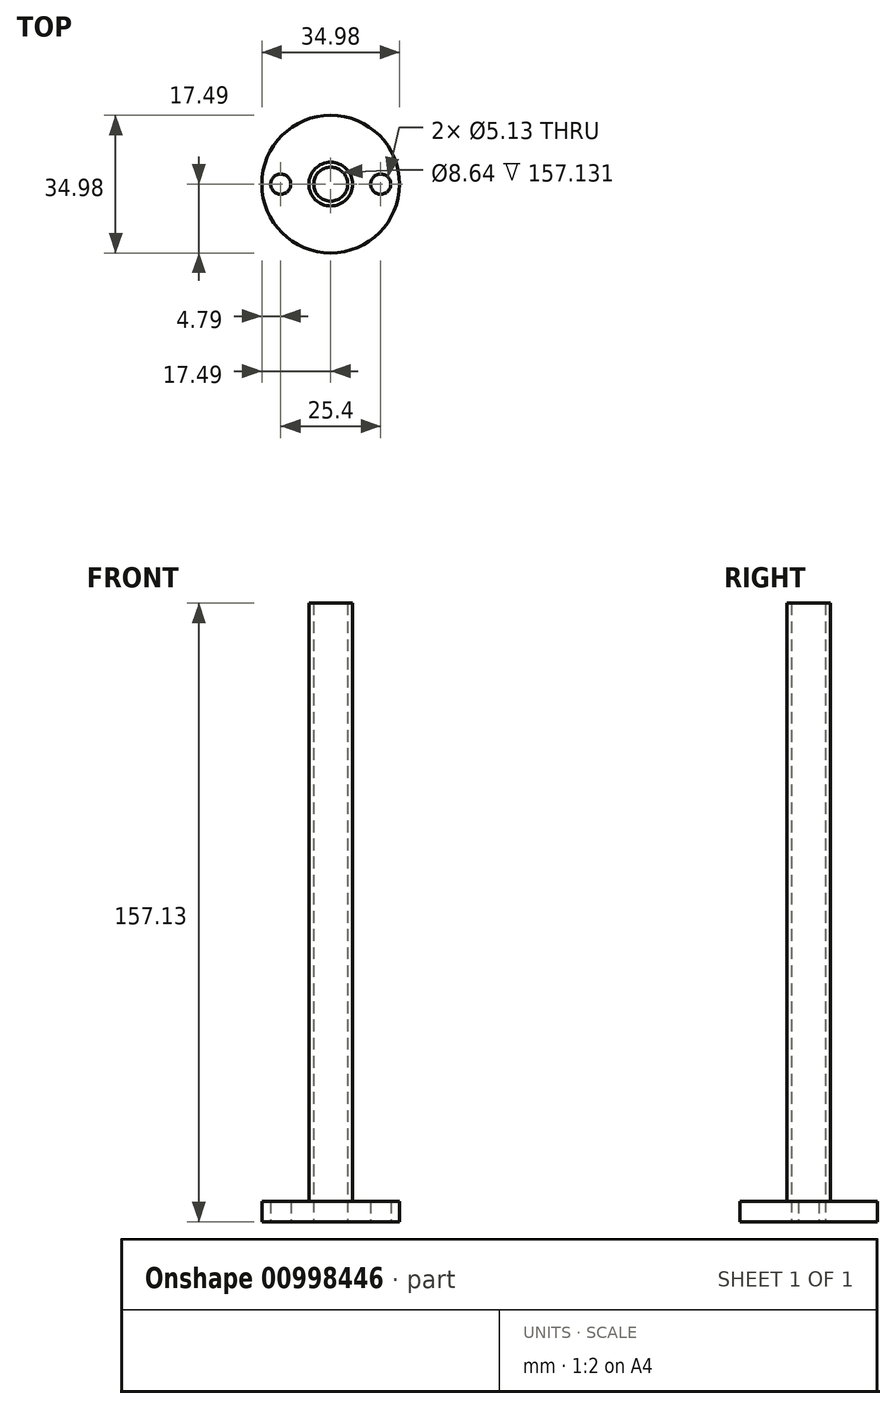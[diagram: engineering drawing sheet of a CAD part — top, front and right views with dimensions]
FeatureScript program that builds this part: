
annotation { "Feature Type Name" : "Feature", "Feature Type Description" : "" }
export const myFeature = defineFeature(function(context is Context, id is Id, definition is map)
    precondition{}
    {
        {
            var Q0;
            Q0=qCreatedBy(makeId("Top.planeOp"),FACE);
            var sketch = newSketch(context, id + "F0", { "sketchPlane" : qUnion([Q0])});
            skCircle(sketch, "E0", {"center": v(0, 0) * mm, "radius": 17.5 * mm});
            skSolve(sketch);
        }
        {
            var Q0;
            Q0 = qSketchRegion(id + "F0", true);
            extrude(context, id + "F1", {"entities" : qUnion([Q0]), "depth" : 5.13 * mm, "offsetDistance" : 25.4 * mm});
        }
        {
            var Q0;
            Q0=makeQuery(id+"F1.opExtrude","CAP_FACE",FACE,{"disambiguationData":[OSD([sQuery(id+"F0.wireOp",EDGE,"E0")])],"isStart":false});
            var sketch = newSketch(context, id + "F2", { "sketchPlane" : qUnion([Q0])});
            skCircle(sketch, "E1", {"center": v(0, 0) * mm, "radius": 5.56 * mm});
            skSolve(sketch);
        }
        {
            var Q0;
            Q0=makeQuery(id+"F2.imprint","IMPRINT",FACE,{"disambiguationData":[TD([[makeQuery(id+"F2.imprint","IMPRINT",EDGE,{"derivedFrom":sQuery(id+"F2.wireOp",EDGE,"E1")}),1.0]])]});
            extrude(context, id + "F3", {"entities" : qUnion([Q0]), "operationType" : NewBodyOperationType.ADD, "depth" : 152 * mm, "offsetDistance" : 25.4 * mm});
        }
        {
            var Q0;
            Q0=makeQuery(id+"F1.opExtrude","CAP_FACE",FACE,{"disambiguationData":[OSD([sQuery(id+"F0.wireOp",EDGE,"E0")])],"isStart":true});
            var sketch = newSketch(context, id + "F4", { "sketchPlane" : qUnion([Q0])});
            skCircle(sketch, "E2", {"center": v(0, 0) * mm, "radius": 4.32 * mm});
            skSolve(sketch);
        }
        {
            var Q0;
            Q0 = qSketchRegion(id + "F4", true);
            extrude(context, id + "F5", {"entities" : qUnion([Q0]), "operationType" : NewBodyOperationType.REMOVE, "endBound" : BoundingType.THROUGH_ALL, "oppositeDirection" : true, "depth" : 25.4 * mm, "offsetDistance" : 25.4 * mm});
        }
        {
            var Q0;
            Q0=makeQuery(id+"F1.opExtrude","CAP_FACE",FACE,{"disambiguationData":[OSD([sQuery(id+"F0.wireOp",EDGE,"E0")])],"isStart":true});
            var sketch = newSketch(context, id + "F6", { "sketchPlane" : qUnion([Q0])});
            skPoint(sketch, "E3", {"position": v(-12.7, 0) * mm});
            skPoint(sketch, "E4", {"position": v(12.7, 0) * mm});
            skSolve(sketch);
        }
        {
            var Q0;
            Q0=sQuery(id+"F6.wireOp",VERTEX,"E3");
            var Q1;
            Q1=sQuery(id+"F6.wireOp",VERTEX,"E4");
            var Q2;
            Q2=makeQuery(id+"F1.opExtrude","SWEPT_BODY",BODY,{"disambiguationData":[OSD([sQuery(id+"F0.wireOp",EDGE,"E0")])]});
            hole(context, id + "F7", {"style" : HoleStyle.SIMPLE, "endStyle" : HoleEndStyle.THROUGH, "holeDiameter" : 5.13 * mm, "majorDiameter" : 6.35 * mm, "isTappedThrough" : true, "tappedDepth" : 12.7 * mm, "tapClearance" : 3, "locations" : qUnion([Q0, Q1]), "scope" : qUnion([Q2])});
        }
    });
